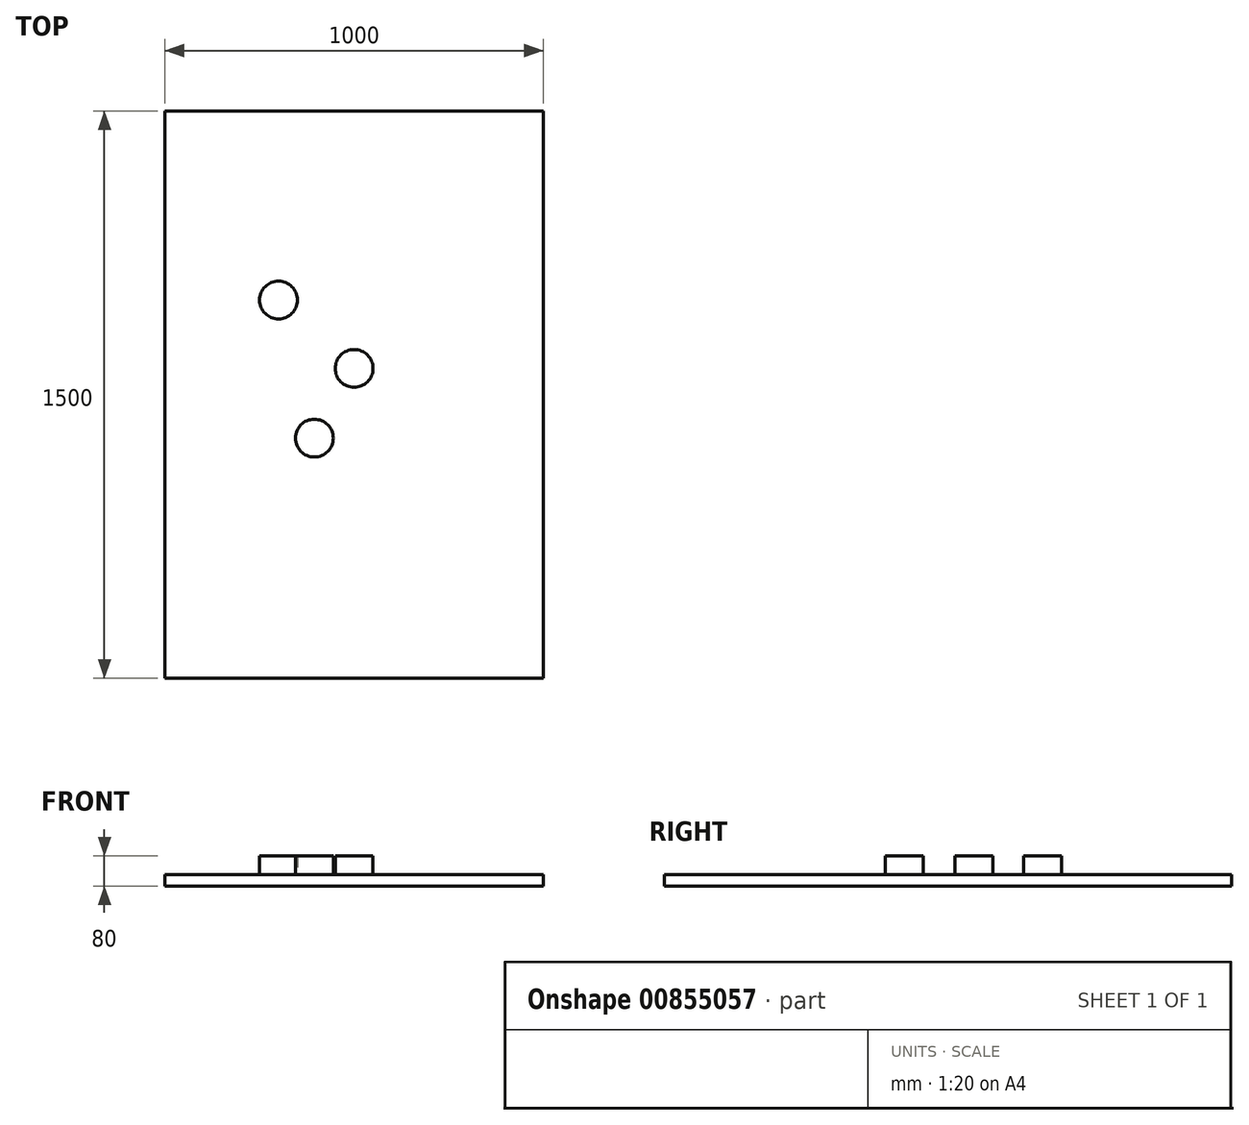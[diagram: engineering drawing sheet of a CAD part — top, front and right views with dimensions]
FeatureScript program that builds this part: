
annotation { "Feature Type Name" : "Feature", "Feature Type Description" : "" }
export const myFeature = defineFeature(function(context is Context, id is Id, definition is map)
    precondition{}
    {
        {
            var Q0;
            Q0=qCreatedBy(makeId("Top.planeOp"),FACE);
            var sketch = newSketch(context, id + "F0", { "sketchPlane" : qUnion([Q0])});
            skLineSegment(sketch, "E0.bottom", {"start": v(500, 750) * mm, "end": v(-500, 750) * mm});
            skLineSegment(sketch, "E0.top", {"start": v(500, -750) * mm, "end": v(-500, -750) * mm});
            skLineSegment(sketch, "E0.left", {"start": v(500, 750) * mm, "end": v(500, -750) * mm});
            skLineSegment(sketch, "E0.right", {"start": v(-500, 750) * mm, "end": v(-500, -750) * mm});
            skPoint(sketch, "E0.middle", {"position": v(0, 0) * mm});
            skSolve(sketch);
        }
        {
            var Q0;
            Q0 = qSketchRegion(id + "F0", true);
            extrude(context, id + "F1", {"entities" : qUnion([Q0]), "depth" : 30 * mm, "offsetDistance" : 25 * mm});
        }
        {
            var Q0;
            Q0=makeQuery(id+"F1.opExtrude","CAP_FACE",FACE,{"disambiguationData":[OSD([sQuery(id+"F0.wireOp",EDGE,"E0.bottom"),sQuery(id+"F0.wireOp",EDGE,"E0.top"),sQuery(id+"F0.wireOp",EDGE,"E0.left"),sQuery(id+"F0.wireOp",EDGE,"E0.right")])],"isStart":false});
            var sketch = newSketch(context, id + "F2", { "sketchPlane" : qUnion([Q0])});
            skCircle(sketch, "E1", {"center": v(-200, 250) * mm, "radius": 50 * mm});
            skCircle(sketch, "E2", {"center": v(0, 69.21) * mm, "radius": 50 * mm});
            skCircle(sketch, "E3", {"center": v(-105.18, -115.22) * mm, "radius": 50 * mm});
            skSolve(sketch);
        }
        {
            var Q0;
            Q0=makeQuery(id+"F2.imprint","IMPRINT",FACE,{"disambiguationData":[TD([[makeQuery(id+"F2.imprint","IMPRINT",EDGE,{"derivedFrom":sQuery(id+"F2.wireOp",EDGE,"E1")}),1.0]])]});
            var Q1;
            Q1=makeQuery(id+"F2.imprint","IMPRINT",FACE,{"disambiguationData":[TD([[makeQuery(id+"F2.imprint","IMPRINT",EDGE,{"derivedFrom":sQuery(id+"F2.wireOp",EDGE,"E2")}),1.0]])]});
            var Q2;
            Q2=makeQuery(id+"F2.imprint","IMPRINT",FACE,{"disambiguationData":[TD([[makeQuery(id+"F2.imprint","IMPRINT",EDGE,{"derivedFrom":sQuery(id+"F2.wireOp",EDGE,"E3")}),1.0]])]});
            extrude(context, id + "F3", {"entities" : qUnion([Q0, Q1, Q2]), "operationType" : NewBodyOperationType.ADD, "depth" : 50 * mm, "offsetDistance" : 25 * mm});
        }
    });
